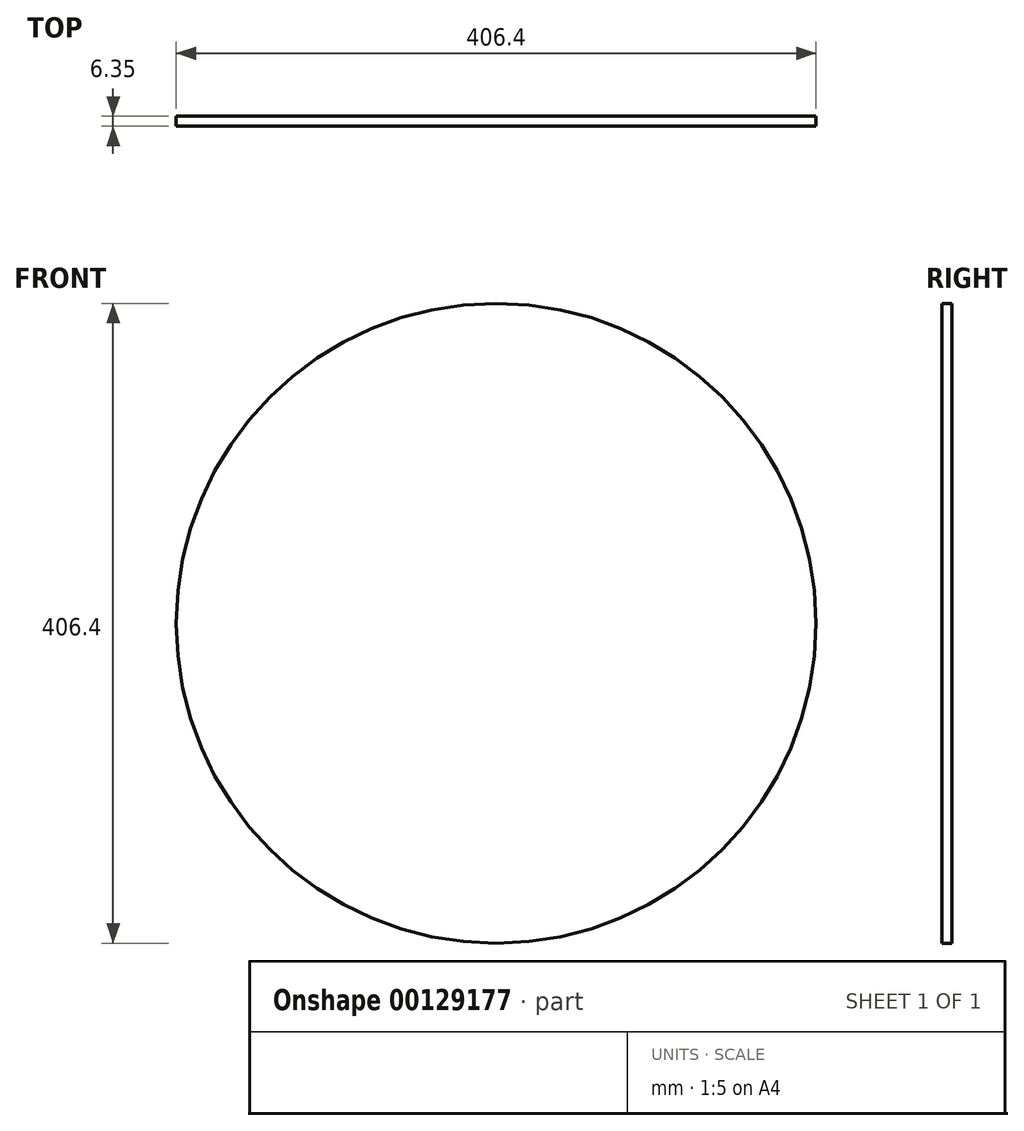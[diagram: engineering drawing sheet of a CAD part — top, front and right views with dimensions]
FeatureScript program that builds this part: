
annotation { "Feature Type Name" : "Feature", "Feature Type Description" : "" }
export const myFeature = defineFeature(function(context is Context, id is Id, definition is map)
    precondition{}
    {
        {
            var Q0;
            Q0=qCreatedBy(makeId("Front.planeOp"),FACE);
            var sketch = newSketch(context, id + "F0", { "sketchPlane" : qUnion([Q0])});
            skCircle(sketch, "E0", {"center": v(0, 0) * mm, "radius": 203.2 * mm});
            skSolve(sketch);
        }
        {
            var Q0;
            Q0 = qSketchRegion(id + "F0", true);
            extrude(context, id + "F1", {"entities" : qUnion([Q0]), "depth" : 6.35 * mm});
        }
    });
